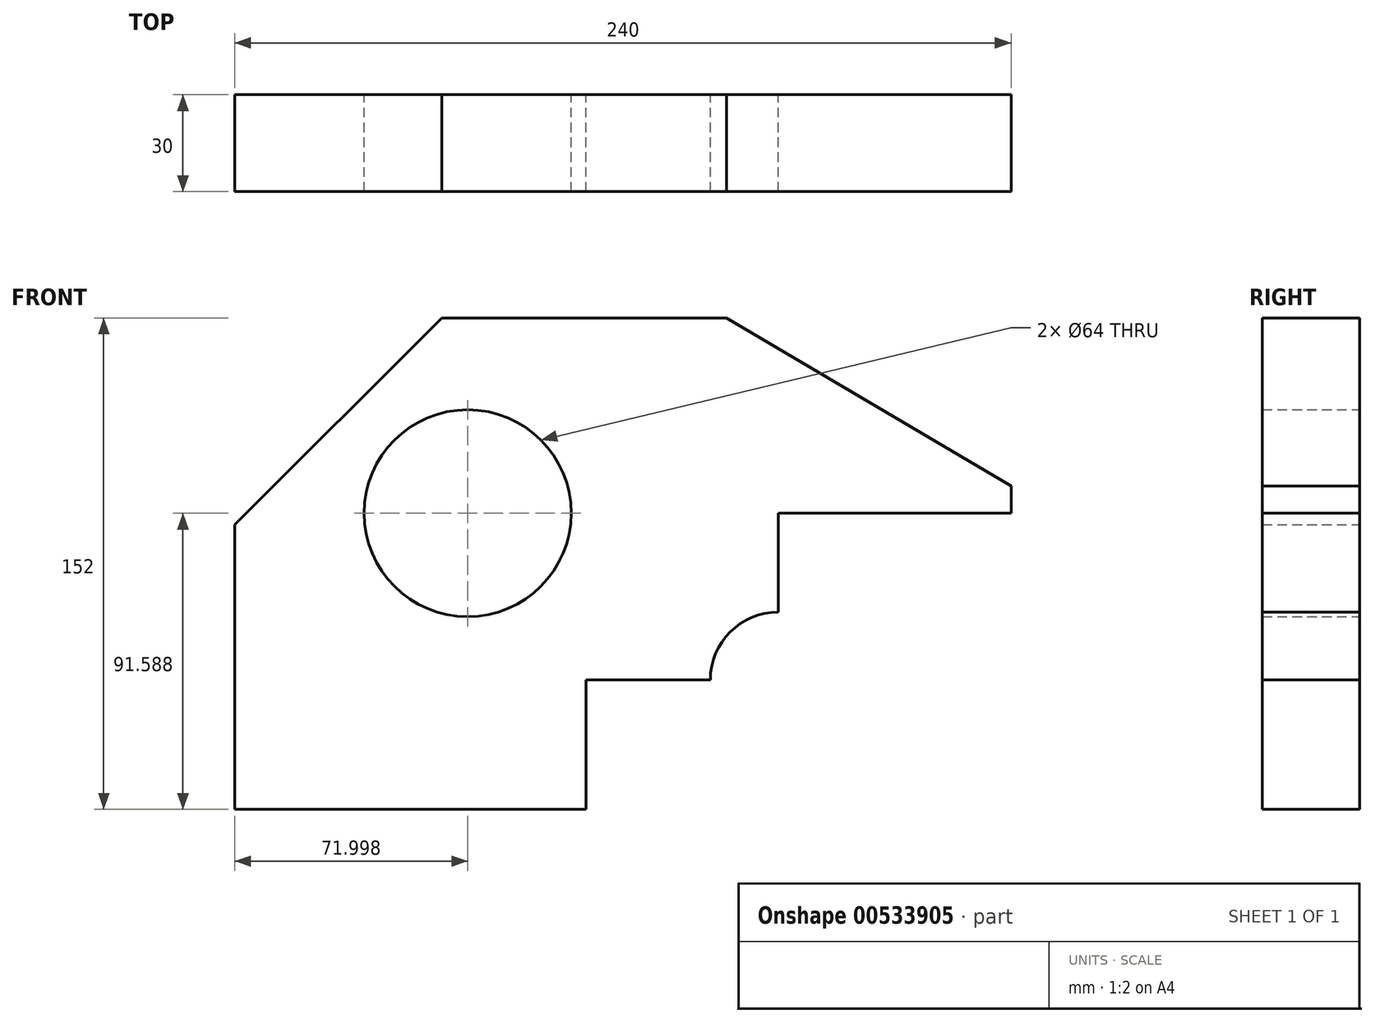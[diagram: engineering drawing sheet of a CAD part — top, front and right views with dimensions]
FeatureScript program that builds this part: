
annotation { "Feature Type Name" : "Feature", "Feature Type Description" : "" }
export const myFeature = defineFeature(function(context is Context, id is Id, definition is map)
    precondition{}
    {
        {
            var Q0;
            Q0=qCreatedBy(makeId("Front.planeOp"),FACE);
            var sketch = newSketch(context, id + "F0", { "sketchPlane" : qUnion([Q0])});
            skLineSegment(sketch, "E0", {"start": v(-123.02, -58.91) * mm, "end": v(116.98, -58.91) * mm});
            skLineSegment(sketch, "E1", {"start": v(116.98, 41.09) * mm, "end": v(116.98, -58.91) * mm});
            skLineSegment(sketch, "E2", {"start": v(-123.02, -58.91) * mm, "end": v(-123.02, 29.09) * mm});
            skLineSegment(sketch, "E3", {"start": v(-123.02, 29.09) * mm, "end": v(-59.02, 93.09) * mm});
            skLineSegment(sketch, "E4", {"start": v(-59.02, 93.09) * mm, "end": v(28.98, 93.09) * mm});
            skLineSegment(sketch, "E5", {"start": v(28.98, 93.09) * mm, "end": v(116.98, 41.09) * mm});
            skCircle(sketch, "E6", {"center": v(44.98, -18.91) * mm, "radius": 21 * mm});
            skLineSegment(sketch, "E7", {"start": v(23.98, -18.91) * mm, "end": v(-14.38, -18.91) * mm});
            skLineSegment(sketch, "E8", {"start": v(-14.38, -18.91) * mm, "end": v(23.98, -18.91) * mm});
            skLineSegment(sketch, "E9", {"start": v(44.98, 2.09) * mm, "end": v(44.98, 32.68) * mm});
            skLineSegment(sketch, "E10", {"start": v(-14.38, -18.91) * mm, "end": v(-14.38, -58.91) * mm});
            skLineSegment(sketch, "E11", {"start": v(116.98, 32.68) * mm, "end": v(44.98, 32.68) * mm});
            skCircle(sketch, "E12", {"center": v(-51.02, 32.68) * mm, "radius": 32 * mm});
            skLineSegment(sketch, "E13", {"start": v(-19.02, 32.68) * mm, "end": v(44.98, 32.68) * mm});
            skSolve(sketch);
        }
        {
            var Q0;
            {var subQ5=sQuery(id+"F0.wireOp",EDGE,"E2");Q0=makeQuery(id+"F0.imprint","IMPRINT",FACE,{"disambiguationData":[TD([[makeQuery(id+"F0.imprint","IMPRINT",EDGE,{"derivedFrom":subQ5}),-1.0]])]});}
            var Q1;
            {var subQ0=sQuery(id+"F0.wireOp",EDGE,"E8");Q1=makeQuery(id+"F0.imprint","IMPRINT",FACE,{"disambiguationData":[TD([[makeQuery(id+"F0.imprint","IMPRINT",EDGE,{"derivedFrom":subQ0}),-1.0]])]});}
            extrude(context, id + "F1", {"entities" : qUnion([Q0, Q1]), "depth" : 30 * mm, "offsetDistance" : 25 * mm});
        }
    });
